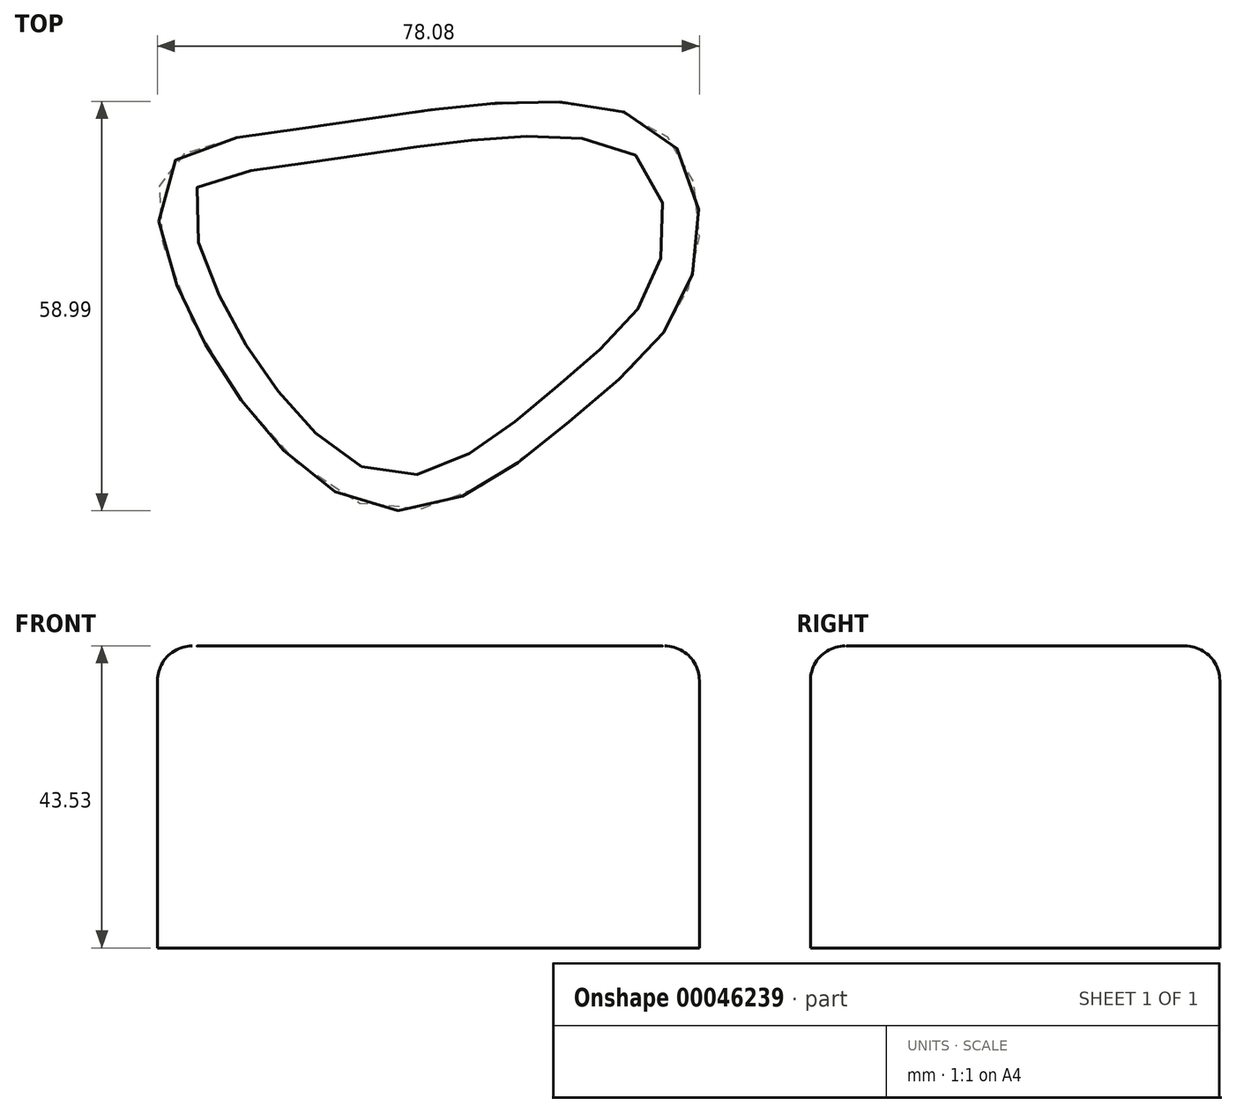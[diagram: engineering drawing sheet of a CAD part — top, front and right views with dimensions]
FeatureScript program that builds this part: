
annotation { "Feature Type Name" : "Feature", "Feature Type Description" : "" }
export const myFeature = defineFeature(function(context is Context, id is Id, definition is map)
    precondition{}
    {
        {
            var Q0;
            Q0=qCreatedBy(makeId("Top.planeOp"),FACE);
            var sketch = newSketch(context, id + "F0", { "sketchPlane" : qUnion([Q0])});
            skFitSpline(sketch, "E0", {"points": [v(-19.93, 36.08) * mm, v(30.88, 36.36) * mm, v(35.94, 13.9) * mm, v(19.37, -5.47) * mm, v(-12.07, -17.83) * mm, v(-40.7, 26.81) * mm, v(-19.93, 36.08) * mm]});
            skSolve(sketch);
        }
        {
            var Q0;
            Q0=makeQuery(id+"F0.imprint","IMPRINT",FACE,{"disambiguationData":[TD([[makeQuery(id+"F0.imprint","IMPRINT",EDGE,{"derivedFrom":sQuery(id+"F0.wireOp",EDGE,"E0")}),-1.0]])]});
            extrude(context, id + "F1", {"entities" : qUnion([Q0]), "depth" : 43.53 * mm});
        }
        {
            var Q0;
            Q0=makeQuery(id+"F1.opExtrude","CAP_EDGE",EDGE,{"disambiguationData":[OSD([sQuery(id+"F0.wireOp",EDGE,"E0")])],"isStart":false});
            fillet(context, id + "F2", {"entities" : qUnion([Q0]), "radius" : 5 * mm, "tangentPropagation" : true, "allowEdgeOverflow" : false});
        }
    });
